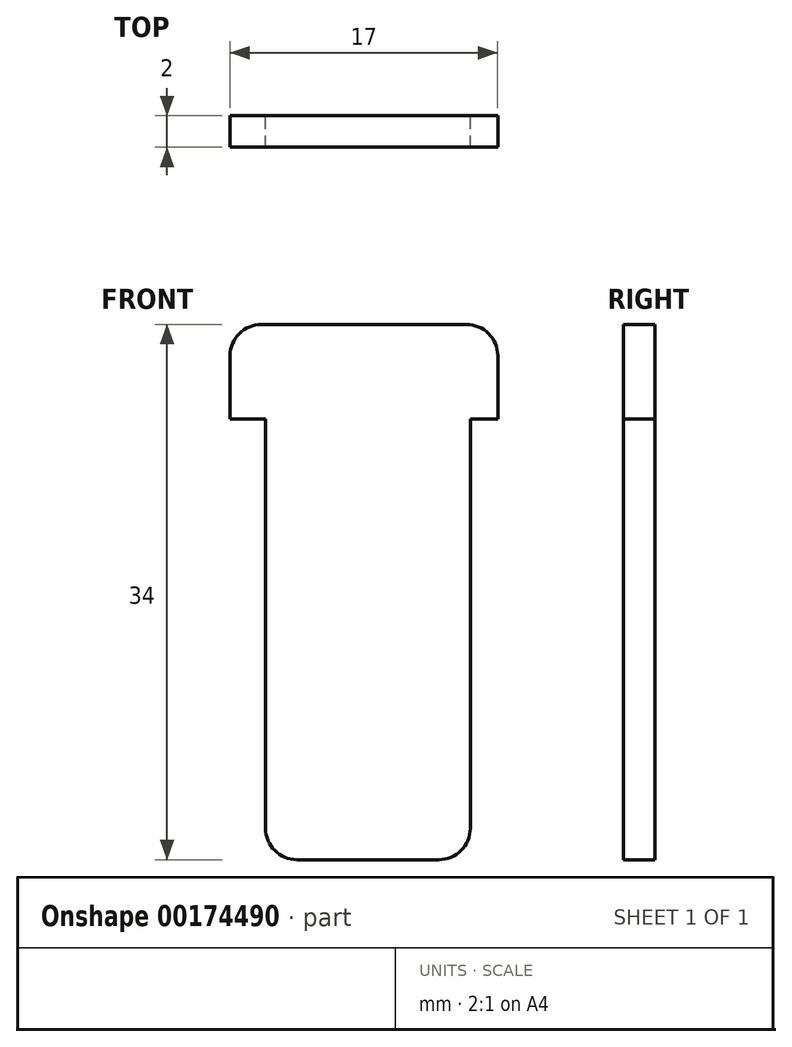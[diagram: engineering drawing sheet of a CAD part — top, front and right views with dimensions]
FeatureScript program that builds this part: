
annotation { "Feature Type Name" : "Feature", "Feature Type Description" : "" }
export const myFeature = defineFeature(function(context is Context, id is Id, definition is map)
    precondition{}
    {
        {
            var Q0;
            Q0=qCreatedBy(makeId("Front.planeOp"),FACE);
            var sketch = newSketch(context, id + "F0", { "sketchPlane" : qUnion([Q0])});
            skLineSegment(sketch, "E0.bottom", {"start": v(-6.21, 10.6) * mm, "end": v(6.79, 10.6) * mm});
            skLineSegment(sketch, "E0.top", {"start": v(-6.21, -17.4) * mm, "end": v(6.79, -17.4) * mm});
            skLineSegment(sketch, "E0.left", {"start": v(-6.21, 10.6) * mm, "end": v(-6.21, -17.4) * mm});
            skLineSegment(sketch, "E0.right", {"start": v(6.79, 10.6) * mm, "end": v(6.79, -17.4) * mm});
            skLineSegment(sketch, "E1.bottom", {"start": v(-8.47, 16.6) * mm, "end": v(8.53, 16.6) * mm});
            skLineSegment(sketch, "E1.top", {"start": v(-8.47, 10.6) * mm, "end": v(8.53, 10.6) * mm});
            skLineSegment(sketch, "E1.left", {"start": v(-8.47, 16.6) * mm, "end": v(-8.47, 10.6) * mm});
            skLineSegment(sketch, "E1.right", {"start": v(8.53, 16.6) * mm, "end": v(8.53, 10.6) * mm});
            skSolve(sketch);
        }
        {
            var Q0;
            Q0 = qSketchRegion(id + "F0", true);
            extrude(context, id + "F1", {"entities" : qUnion([Q0]), "depth" : 2 * mm});
        }
        {
            var Q0;
            Q0=makeQuery(id+"F1.opExtrude","SWEPT_EDGE",EDGE,{"disambiguationData":[OSD([sQuery(id+"F0.wireOp",EDGE,"E1.bottom"),sQuery(id+"F0.wireOp",EDGE,"E1.left")])]});
            var Q1;
            Q1=makeQuery(id+"F1.opExtrude","SWEPT_EDGE",EDGE,{"disambiguationData":[OSD([sQuery(id+"F0.wireOp",EDGE,"E0.top"),sQuery(id+"F0.wireOp",EDGE,"E0.left")])]});
            fillet(context, id + "F2", {"entities" : qUnion([Q0, Q1]), "radius" : 2 * mm, "tangentPropagation" : true, "allowEdgeOverflow" : false});
        }
        {
            var Q0;
            Q0=makeQuery(id+"F1.opExtrude","SWEPT_EDGE",EDGE,{"disambiguationData":[OSD([sQuery(id+"F0.wireOp",EDGE,"E1.bottom"),sQuery(id+"F0.wireOp",EDGE,"E1.right")])]});
            var Q1;
            Q1=makeQuery(id+"F1.opExtrude","SWEPT_EDGE",EDGE,{"disambiguationData":[OSD([sQuery(id+"F0.wireOp",EDGE,"E0.top"),sQuery(id+"F0.wireOp",EDGE,"E0.right")])]});
            fillet(context, id + "F3", {"entities" : qUnion([Q0, Q1]), "radius" : 2 * mm, "tangentPropagation" : true, "allowEdgeOverflow" : false});
        }
    });
